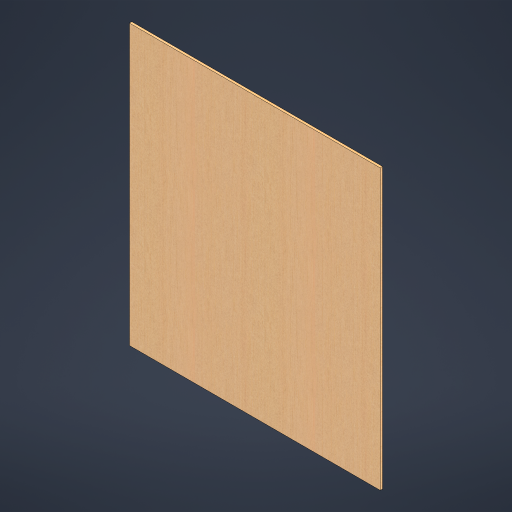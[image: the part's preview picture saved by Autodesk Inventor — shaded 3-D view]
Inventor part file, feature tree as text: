
AUTODESK INVENTOR PART (.ipt)
format: ipt  version: 2024 (Build 280153000, 153)  size: 314,880 bytes
history: native  units: mm
features: other x2, extrude x1, sketch x1
ambient origin geometry x8: Origin, YZ Plane, XZ Plane, XY Plane, X Axis, Y Axis, Z Axis, Center Point
bodies: Body1 (feature_tree)
feature tree (4):
  other  "솔리드1"
  extrude  "돌출1"  Depth=530.0mm
  sketch  "스케치1"
  other  "Finish1"
